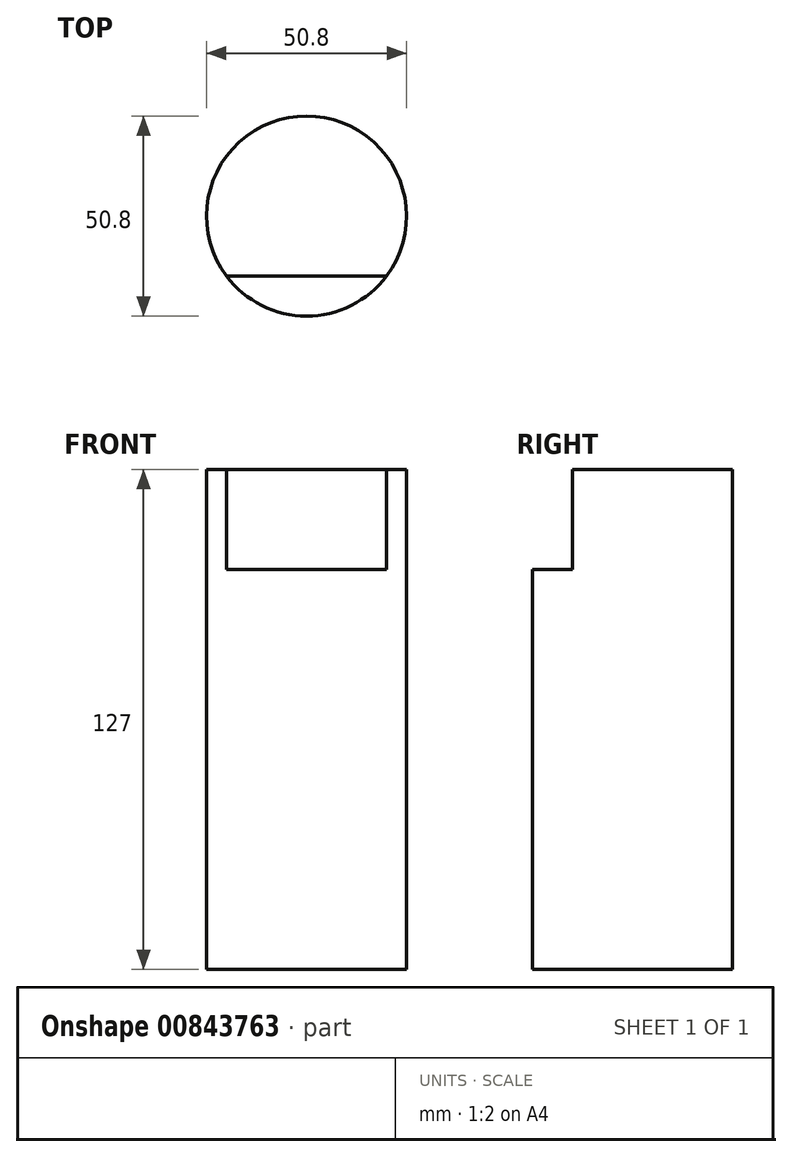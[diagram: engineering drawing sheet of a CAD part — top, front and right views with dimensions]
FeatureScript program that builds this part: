
annotation { "Feature Type Name" : "Feature", "Feature Type Description" : "" }
export const myFeature = defineFeature(function(context is Context, id is Id, definition is map)
    precondition{}
    {
        {
            var Q0;
            Q0=qCreatedBy(makeId("Top.planeOp"),FACE);
            var sketch = newSketch(context, id + "F0", { "sketchPlane" : qUnion([Q0])});
            skCircle(sketch, "E0", {"center": v(0, 0) * mm, "radius": 25.4 * mm});
            skSolve(sketch);
        }
        {
            var Q0;
            Q0 = qSketchRegion(id + "F0", true);
            extrude(context, id + "F1", {"entities" : qUnion([Q0]), "depth" : 127 * mm, "offsetDistance" : 25.4 * mm});
        }
        {
            var Q0;
            Q0=makeQuery(id+"F1.opExtrude","CAP_FACE",FACE,{"disambiguationData":[OSD([sQuery(id+"F0.wireOp",EDGE,"E0")])],"isStart":false});
            var sketch = newSketch(context, id + "F2", { "sketchPlane" : qUnion([Q0])});
            skLineSegment(sketch, "E1", {"start": v(0, -25.4) * mm, "end": v(0, -15.24) * mm, "construction": true});
            skLineSegment(sketch, "E2", {"start": v(0, -15.24) * mm, "end": v(20.32, -15.24) * mm});
            skLineSegment(sketch, "E3", {"start": v(20.32, -15.24) * mm, "end": v(-20.32, -15.24) * mm});
            skArc(sketch, "E4", {"start": v(20.32, -15.24) * mm, "mid": v(0, -25.4) * mm, "end": v(-20.32, -15.24) * mm});
            skSolve(sketch);
        }
        {
            var Q0;
            Q0 = qSketchRegion(id + "F2", true);
            extrude(context, id + "F3", {"entities" : qUnion([Q0]), "operationType" : NewBodyOperationType.REMOVE, "oppositeDirection" : true, "depth" : 25.4 * mm, "offsetDistance" : 25.4 * mm});
        }
    });
